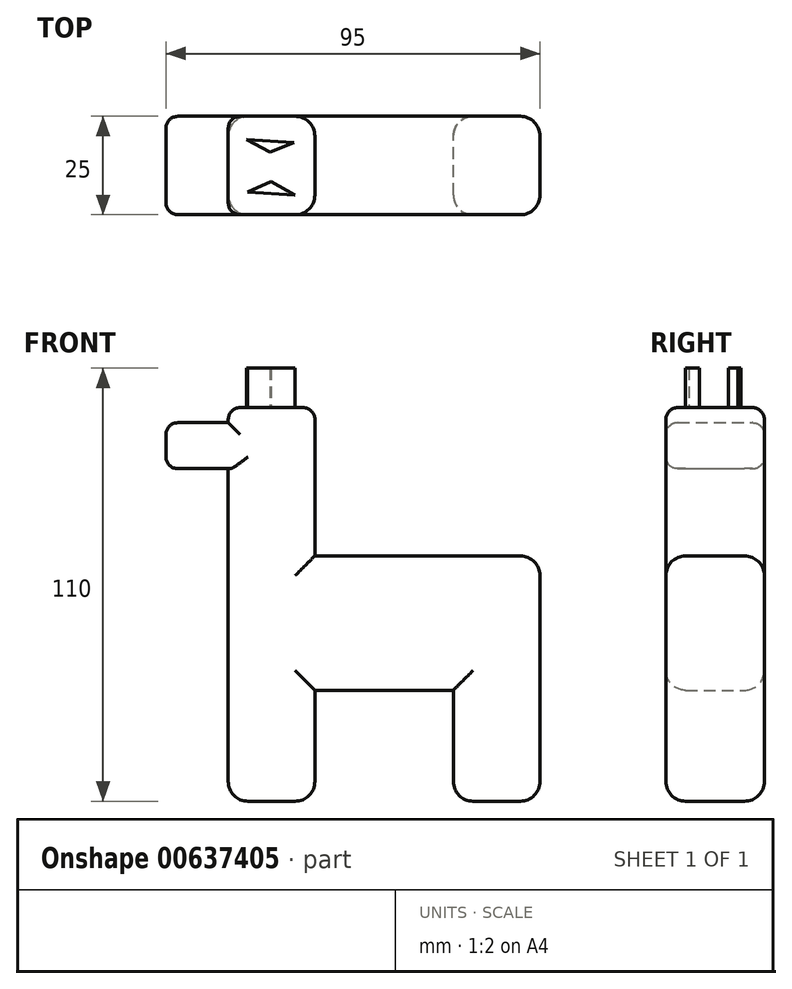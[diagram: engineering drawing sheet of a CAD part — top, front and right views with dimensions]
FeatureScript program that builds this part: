
annotation { "Feature Type Name" : "Feature", "Feature Type Description" : "" }
export const myFeature = defineFeature(function(context is Context, id is Id, definition is map)
    precondition{}
    {
        {
            var Q0;
            Q0=qCreatedBy(makeId("Front.planeOp"),FACE);
            var sketch = newSketch(context, id + "F0", { "sketchPlane" : qUnion([Q0])});
            skLineSegment(sketch, "E0", {"start": v(-57.2, -28.18) * mm, "end": v(-35.2, -28.18) * mm});
            skLineSegment(sketch, "E1", {"start": v(-35.2, -28.18) * mm, "end": v(-35.2, 0) * mm});
            skLineSegment(sketch, "E2", {"start": v(-35.2, 0) * mm, "end": v(0, 0) * mm});
            skLineSegment(sketch, "E3", {"start": v(0, 0) * mm, "end": v(0, -28.18) * mm});
            skLineSegment(sketch, "E4", {"start": v(0, -28.18) * mm, "end": v(22, -28.18) * mm});
            skPoint(sketch, "E4.endSnap0", {"position": v(-46.2, -28.18) * mm});
            skLineSegment(sketch, "E5", {"start": v(22, -28.18) * mm, "end": v(22, 0) * mm});
            skLineSegment(sketch, "E6", {"start": v(22, 0) * mm, "end": v(22, 34.14) * mm});
            skLineSegment(sketch, "E7", {"start": v(22, 34.14) * mm, "end": v(-35.2, 34.14) * mm});
            skLineSegment(sketch, "E8", {"start": v(-35.2, 34.14) * mm, "end": v(-35.2, 71.82) * mm});
            skLineSegment(sketch, "E9", {"start": v(-35.2, 71.82) * mm, "end": v(-57.2, 71.82) * mm});
            skLineSegment(sketch, "E10", {"start": v(-57.2, 71.82) * mm, "end": v(-57.2, 67.98) * mm});
            skLineSegment(sketch, "E11", {"start": v(-57.2, 67.98) * mm, "end": v(-73, 67.98) * mm});
            skLineSegment(sketch, "E12", {"start": v(-73, 67.98) * mm, "end": v(-73, 56.29) * mm});
            skLineSegment(sketch, "E13", {"start": v(-73, 56.29) * mm, "end": v(-57.2, 56.29) * mm});
            skLineSegment(sketch, "E14", {"start": v(-57.2, 56.29) * mm, "end": v(-57.2, -28.18) * mm});
            skSolve(sketch);
        }
        {
            var Q0;
            Q0 = qSketchRegion(id + "F0", true);
            extrude(context, id + "F1", {"entities" : qUnion([Q0]), "depth" : 25 * mm, "offsetDistance" : 25 * mm});
        }
        {
            var Q0;
            Q0=makeQuery(id+"F1.opExtrude","CAP_EDGE",EDGE,{"disambiguationData":[OSD([sQuery(id+"F0.wireOp",EDGE,"E9")])],"isStart":false});
            var Q1;
            Q1=makeQuery(id+"F1.opExtrude","SWEPT_EDGE",EDGE,{"disambiguationData":[OSD([sQuery(id+"F0.wireOp",EDGE,"E8"),sQuery(id+"F0.wireOp",EDGE,"E9")])]});
            var Q2;
            Q2=makeQuery(id+"F1.opExtrude","CAP_EDGE",EDGE,{"disambiguationData":[OSD([sQuery(id+"F0.wireOp",EDGE,"E9")])],"isStart":true});
            var Q3;
            Q3=makeQuery(id+"F1.opExtrude","CAP_EDGE",EDGE,{"disambiguationData":[OSD([sQuery(id+"F0.wireOp",EDGE,"E11")])],"isStart":false});
            var Q4;
            Q4=makeQuery(id+"F1.opExtrude","CAP_EDGE",EDGE,{"disambiguationData":[OSD([sQuery(id+"F0.wireOp",EDGE,"E11")])],"isStart":true});
            fillet(context, id + "F2", {"entities" : qUnion([Q0, Q1, Q2, Q3, Q4]), "radius" : 3 * mm, "tangentPropagation" : true, "allowEdgeOverflow" : false});
        }
        {
            var Q0;
            Q0=makeQuery(id+"F1.opExtrude","SWEPT_EDGE",EDGE,{"disambiguationData":[OSD([sQuery(id+"F0.wireOp",EDGE,"E9"),sQuery(id+"F0.wireOp",EDGE,"E10")])]});
            var Q1;
            Q1=makeQuery(id+"F1.opExtrude","SWEPT_EDGE",EDGE,{"disambiguationData":[OSD([sQuery(id+"F0.wireOp",EDGE,"E11"),sQuery(id+"F0.wireOp",EDGE,"E12")])]});
            fillet(context, id + "F3", {"entities" : qUnion([Q0, Q1]), "radius" : 3 * mm, "tangentPropagation" : true, "allowEdgeOverflow" : false});
        }
        {
            var Q0;
            Q0=makeQuery(id+"F1.opExtrude","CAP_EDGE",EDGE,{"disambiguationData":[OSD([sQuery(id+"F0.wireOp",EDGE,"E7")])],"isStart":false});
            var Q1;
            Q1=makeQuery(id+"F1.opExtrude","CAP_EDGE",EDGE,{"disambiguationData":[OSD([sQuery(id+"F0.wireOp",EDGE,"E7")])],"isStart":true});
            var Q2;
            Q2=makeQuery(id+"F1.opExtrude","SWEPT_EDGE",EDGE,{"disambiguationData":[OSD([sQuery(id+"F0.wireOp",EDGE,"E6"),sQuery(id+"F0.wireOp",EDGE,"E7")])]});
            var Q3;
            Q3=makeQuery(id+"F1.opExtrude","CAP_EDGE",EDGE,{"disambiguationData":[OSD([sQuery(id+"F0.wireOp",EDGE,"E5"),sQuery(id+"F0.wireOp",EDGE,"E6")])],"isStart":false});
            var Q4;
            Q4=makeQuery(id+"F1.opExtrude","CAP_EDGE",EDGE,{"disambiguationData":[OSD([sQuery(id+"F0.wireOp",EDGE,"E3")])],"isStart":true});
            var Q5;
            Q5=makeQuery(id+"F1.opExtrude","CAP_EDGE",EDGE,{"disambiguationData":[OSD([sQuery(id+"F0.wireOp",EDGE,"E3")])],"isStart":false});
            var Q6;
            Q6=makeQuery(id+"F1.opExtrude","CAP_EDGE",EDGE,{"disambiguationData":[OSD([sQuery(id+"F0.wireOp",EDGE,"E14")])],"isStart":true});
            var Q7;
            Q7=makeQuery(id+"F1.opExtrude","CAP_EDGE",EDGE,{"disambiguationData":[OSD([sQuery(id+"F0.wireOp",EDGE,"E14")])],"isStart":false});
            var Q8;
            Q8=makeQuery(id+"F1.opExtrude","CAP_EDGE",EDGE,{"disambiguationData":[OSD([sQuery(id+"F0.wireOp",EDGE,"E1")])],"isStart":false});
            var Q9;
            Q9=makeQuery(id+"F1.opExtrude","CAP_EDGE",EDGE,{"disambiguationData":[OSD([sQuery(id+"F0.wireOp",EDGE,"E2")])],"isStart":false});
            var Q10;
            Q10=makeQuery(id+"F1.opExtrude","CAP_EDGE",EDGE,{"disambiguationData":[OSD([sQuery(id+"F0.wireOp",EDGE,"E0")])],"isStart":false});
            var Q11;
            Q11=makeQuery(id+"F1.opExtrude","SWEPT_EDGE",EDGE,{"disambiguationData":[OSD([sQuery(id+"F0.wireOp",EDGE,"E0"),sQuery(id+"F0.wireOp",EDGE,"E14")])]});
            var Q12;
            Q12=makeQuery(id+"F1.opExtrude","CAP_EDGE",EDGE,{"disambiguationData":[OSD([sQuery(id+"F0.wireOp",EDGE,"E4")])],"isStart":false});
            var Q13;
            Q13=makeQuery(id+"F1.opExtrude","CAP_EDGE",EDGE,{"disambiguationData":[OSD([sQuery(id+"F0.wireOp",EDGE,"E2")])],"isStart":true});
            var Q14;
            Q14=makeQuery(id+"F1.opExtrude","CAP_EDGE",EDGE,{"disambiguationData":[OSD([sQuery(id+"F0.wireOp",EDGE,"E1")])],"isStart":true});
            var Q15;
            Q15=makeQuery(id+"F1.opExtrude","SWEPT_EDGE",EDGE,{"disambiguationData":[OSD([sQuery(id+"F0.wireOp",EDGE,"E0"),sQuery(id+"F0.wireOp",EDGE,"E1")])]});
            var Q16;
            Q16=makeQuery(id+"F1.opExtrude","CAP_EDGE",EDGE,{"disambiguationData":[OSD([sQuery(id+"F0.wireOp",EDGE,"E0")])],"isStart":true});
            var Q17;
            Q17=makeQuery(id+"F1.opExtrude","CAP_EDGE",EDGE,{"disambiguationData":[OSD([sQuery(id+"F0.wireOp",EDGE,"E4")])],"isStart":true});
            var Q18;
            Q18=makeQuery(id+"F1.opExtrude","SWEPT_EDGE",EDGE,{"disambiguationData":[OSD([sQuery(id+"F0.wireOp",EDGE,"E4"),sQuery(id+"F0.wireOp",EDGE,"E5")])]});
            var Q19;
            Q19=makeQuery(id+"F1.opExtrude","CAP_EDGE",EDGE,{"disambiguationData":[OSD([sQuery(id+"F0.wireOp",EDGE,"E8")])],"isStart":false});
            var Q20;
            Q20=makeQuery(id+"F1.opExtrude","CAP_EDGE",EDGE,{"disambiguationData":[OSD([sQuery(id+"F0.wireOp",EDGE,"E8")])],"isStart":true});
            var Q21;
            Q21=makeQuery(id+"F1.opExtrude","CAP_EDGE",EDGE,{"disambiguationData":[OSD([sQuery(id+"F0.wireOp",EDGE,"E5"),sQuery(id+"F0.wireOp",EDGE,"E6")])],"isStart":true});
            fillet(context, id + "F4", {"entities" : qUnion([Q0, Q1, Q2, Q3, Q4, Q5, Q6, Q7, Q8, Q9, Q10, Q11, Q12, Q13, Q14, Q15, Q16, Q17, Q18, Q19, Q20, Q21]), "radius" : 5 * mm, "tangentPropagation" : true, "allowEdgeOverflow" : false});
        }
        {
            var Q0;
            Q0=makeQuery(id+"F1.opExtrude","SWEPT_EDGE",EDGE,{"disambiguationData":[OSD([sQuery(id+"F0.wireOp",EDGE,"E12"),sQuery(id+"F0.wireOp",EDGE,"E13")])]});
            fillet(context, id + "F5", {"entities" : qUnion([Q0]), "radius" : 3 * mm, "tangentPropagation" : true, "allowEdgeOverflow" : false});
        }
        {
            var Q0;
            Q0=makeQuery(id+"F1.opExtrude","SWEPT_EDGE",EDGE,{"disambiguationData":[OSD([sQuery(id+"F0.wireOp",EDGE,"E3"),sQuery(id+"F0.wireOp",EDGE,"E4")])]});
            fillet(context, id + "F6", {"entities" : qUnion([Q0]), "radius" : 5 * mm, "tangentPropagation" : true, "allowEdgeOverflow" : false});
        }
        {
            var Q0;
            Q0=makeQuery(id+"F1.opExtrude","SWEPT_FACE",FACE,{"disambiguationData":[OSD([sQuery(id+"F0.wireOp",EDGE,"E9")])]});
            var sketch = newSketch(context, id + "F7", { "sketchPlane" : qUnion([Q0])});
            skLineSegment(sketch, "E15", {"start": v(-52.3, -19.18) * mm, "end": v(-46.33, -16.55) * mm});
            skLineSegment(sketch, "E16", {"start": v(-46.33, -16.55) * mm, "end": v(-40.2, -20) * mm});
            skLineSegment(sketch, "E17", {"start": v(-40.2, -20) * mm, "end": v(-52.3, -19.18) * mm});
            skLineSegment(sketch, "E18", {"start": v(-52.6, -5.9) * mm, "end": v(-46.54, -9.13) * mm});
            skLineSegment(sketch, "E19", {"start": v(-46.54, -9.13) * mm, "end": v(-40.48, -6.72) * mm});
            skLineSegment(sketch, "E20", {"start": v(-40.48, -6.72) * mm, "end": v(-52.6, -5.9) * mm});
            skPoint(sketch, "E21", {"position": v(-46.54, -6.31) * mm});
            skSolve(sketch);
        }
        {
            var Q0;
            Q0 = qSketchRegion(id + "F7", true);
            extrude(context, id + "F8", {"entities" : qUnion([Q0]), "operationType" : NewBodyOperationType.ADD, "depth" : 10 * mm, "offsetDistance" : 25 * mm});
        }
    });
